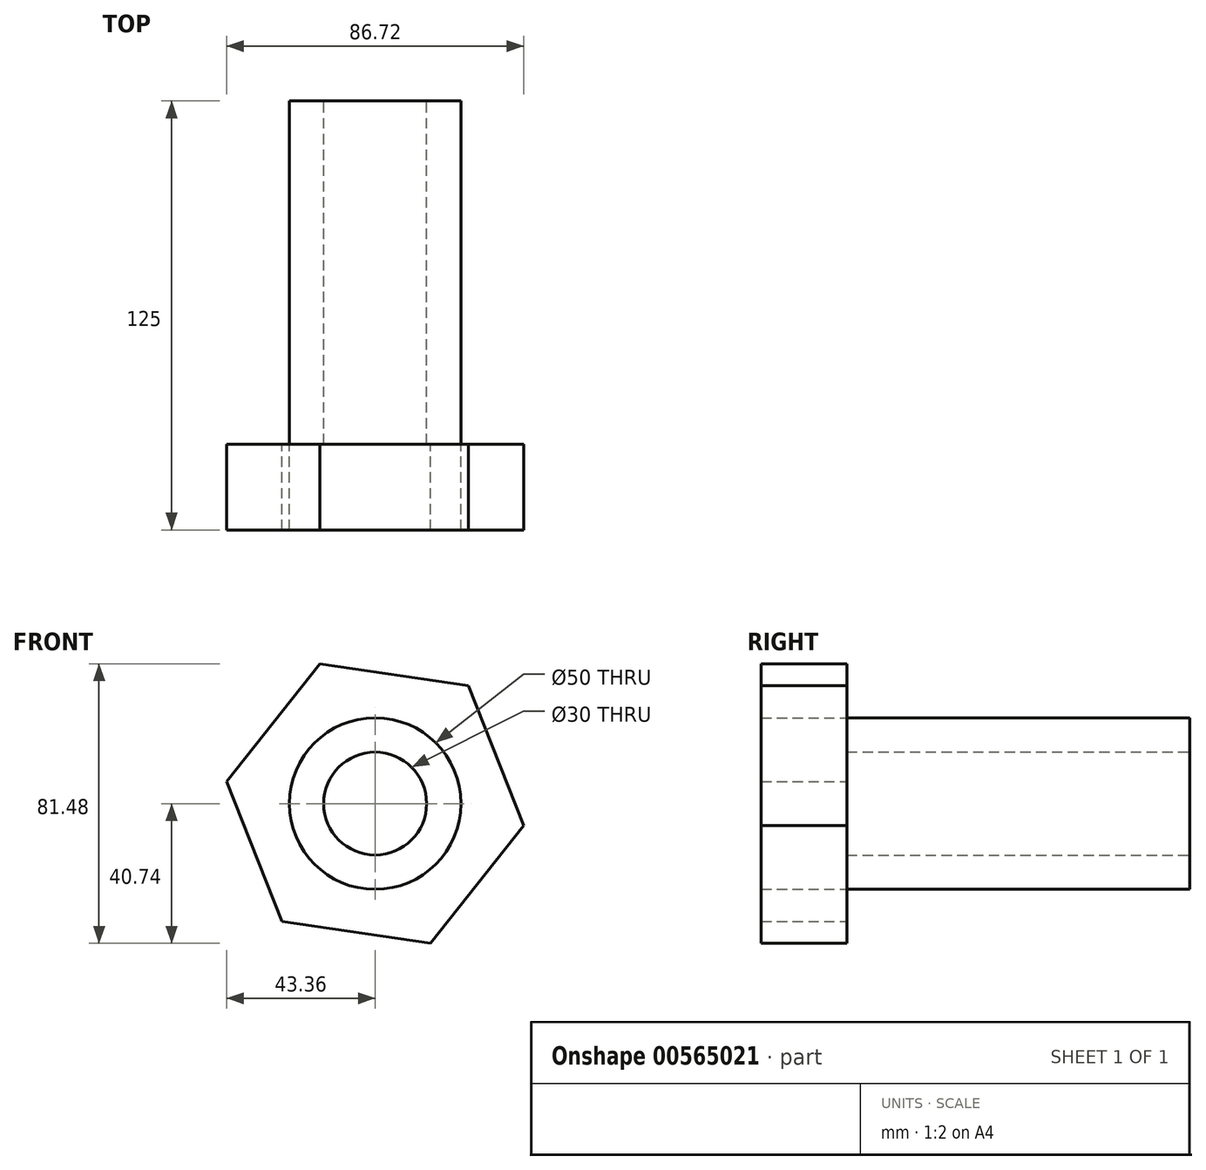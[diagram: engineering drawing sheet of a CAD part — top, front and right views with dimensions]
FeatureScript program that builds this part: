
annotation { "Feature Type Name" : "Feature", "Feature Type Description" : "" }
export const myFeature = defineFeature(function(context is Context, id is Id, definition is map)
    precondition{}
    {
        {
            var Q0;
            Q0=qCreatedBy(makeId("Front.planeOp"),FACE);
            var sketch = newSketch(context, id + "F0", { "sketchPlane" : qUnion([Q0])});
            skCircle(sketch, "E0", {"center": v(0, 0) * mm, "radius": 25 * mm});
            skCircle(sketch, "E1", {"center": v(0, 0) * mm, "radius": 15 * mm});
            skSolve(sketch);
        }
        {
            var Q0;
            Q0=makeQuery(id+"F0.imprint","IMPRINT",FACE,{"disambiguationData":[TD([[makeQuery(id+"F0.imprint","IMPRINT",EDGE,{"derivedFrom":sQuery(id+"F0.wireOp",EDGE,"E0")}),1.0]])]});
            var Q1;
            Q1=makeQuery(id+"F0.imprint","IMPRINT",FACE,{"disambiguationData":[TD([[makeQuery(id+"F0.imprint","IMPRINT",EDGE,{"derivedFrom":sQuery(id+"F0.wireOp",EDGE,"E0")}),1.0]])]});
            var Q2;
            Q2=sQuery(id+"F0.wireOp",EDGE,"E0");
            extrude(context, id + "F1", {"entities" : qUnion([Q0, Q1]), "surfaceEntities" : qUnion([Q2]), "depth" : 100 * mm, "offsetDistance" : 25 * mm});
        }
        {
            var Q0;
            Q0=makeQuery(id+"F1.opExtrude","CAP_FACE",FACE,{"disambiguationData":[OSD([sQuery(id+"F0.wireOp",EDGE,"E0"),sQuery(id+"F0.wireOp",EDGE,"E1")])],"isStart":false});
            var sketch = newSketch(context, id + "F2", { "sketchPlane" : qUnion([Q0])});
            skCircle(sketch, "E2.cCircle", {"center": v(0, 0) * mm, "radius": 37.95 * mm, "construction": true});
            skLineSegment(sketch, "E2.0", {"start": v(43.36, -6.38) * mm, "end": v(16.15, -40.74) * mm});
            skLineSegment(sketch, "E2.1", {"start": v(16.15, -40.74) * mm, "end": v(-27.2, -34.36) * mm});
            skLineSegment(sketch, "E2.2", {"start": v(-27.2, -34.36) * mm, "end": v(-43.36, 6.38) * mm});
            skLineSegment(sketch, "E2.3", {"start": v(-43.36, 6.38) * mm, "end": v(-16.15, 40.74) * mm});
            skLineSegment(sketch, "E2.4", {"start": v(-16.15, 40.74) * mm, "end": v(27.2, 34.36) * mm});
            skLineSegment(sketch, "E2.5", {"start": v(27.2, 34.36) * mm, "end": v(43.36, -6.38) * mm});
            skPoint(sketch, "E2.0.midPoint", {"position": v(29.75, -23.56) * mm});
            skSolve(sketch);
        }
        {
            var Q0;
            Q0=makeQuery(id+"F2.imprint","IMPRINT",FACE,{"disambiguationData":[TD([[makeQuery(id+"F2.imprint","IMPRINT",EDGE,{"derivedFrom":sQuery(id+"F2.wireOp",EDGE,"E2.0")}),-1.0]])]});
            extrude(context, id + "F3", {"entities" : qUnion([Q0]), "depth" : 25 * mm, "offsetDistance" : 25 * mm});
        }
    });
